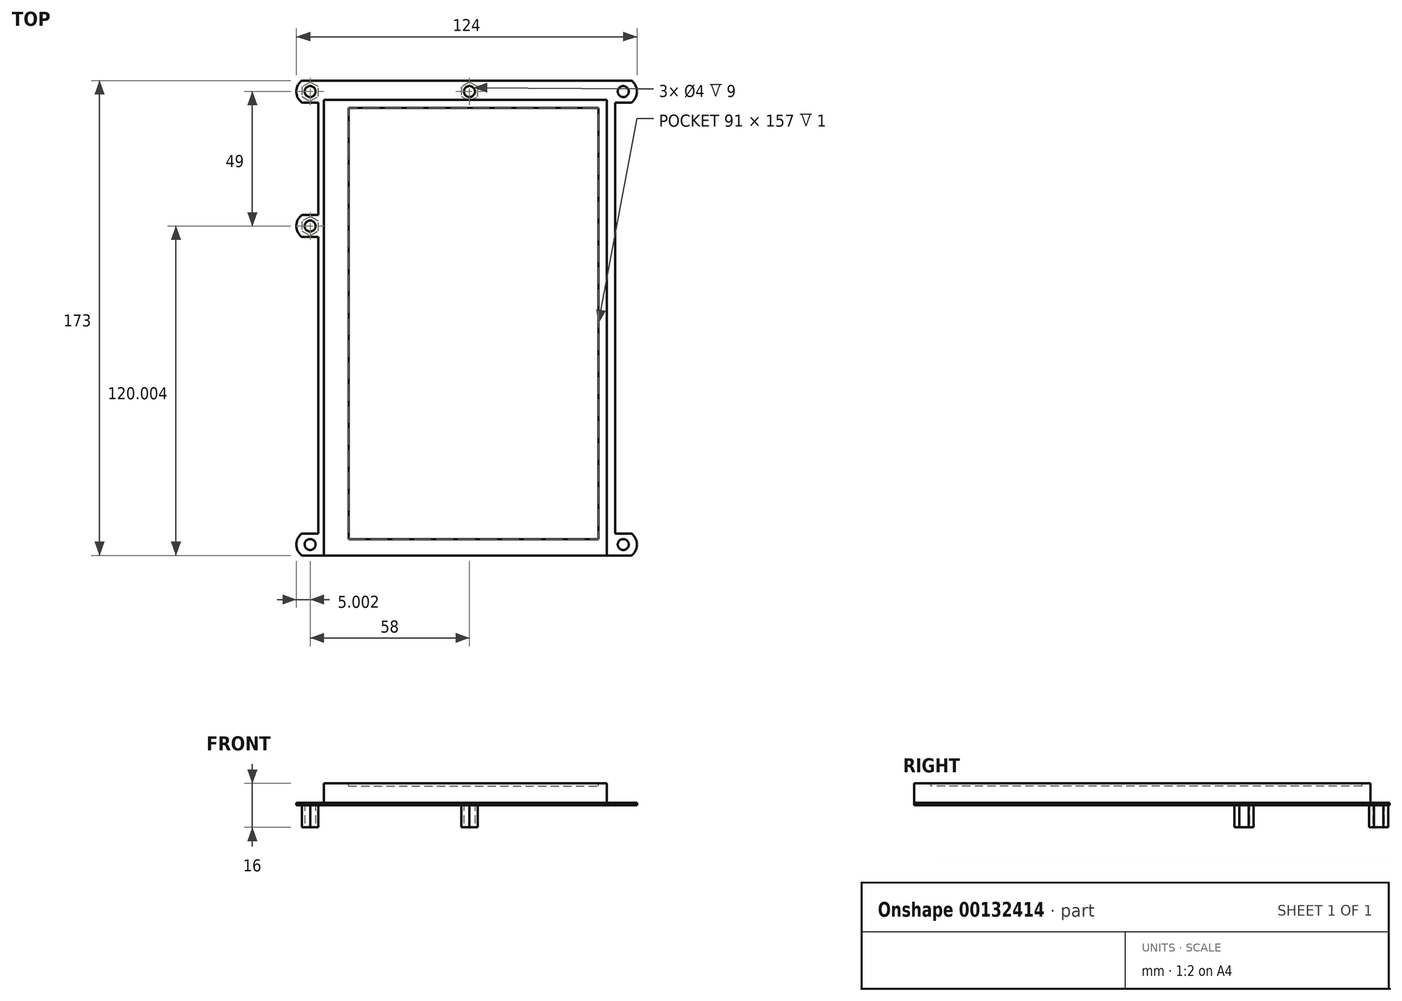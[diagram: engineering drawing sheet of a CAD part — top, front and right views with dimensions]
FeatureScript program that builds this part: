
annotation { "Feature Type Name" : "Feature", "Feature Type Description" : "" }
export const myFeature = defineFeature(function(context is Context, id is Id, definition is map)
    precondition{}
    {
        {
            var Q0;
            Q0=qCreatedBy(makeId("Top.planeOp"),FACE);
            var sketch = newSketch(context, id + "F0", { "sketchPlane" : qUnion([Q0])});
            skLineSegment(sketch, "E0.bottom", {"start": v(-61.72, 83.97) * mm, "end": v(58.28, 83.97) * mm});
            skLineSegment(sketch, "E0.top", {"start": v(-61.72, -89.03) * mm, "end": v(58.28, -89.03) * mm});
            skLineSegment(sketch, "E1", {"start": v(-61.72, -81.03) * mm, "end": v(-55.72, -81.03) * mm});
            skLineSegment(sketch, "E2", {"start": v(-55.72, -81.03) * mm, "end": v(-55.72, 26.97) * mm});
            skLineSegment(sketch, "E3", {"start": v(-55.72, 26.97) * mm, "end": v(-61.72, 26.97) * mm});
            skLineSegment(sketch, "E4", {"start": v(-61.72, 34.97) * mm, "end": v(-55.72, 34.97) * mm});
            skLineSegment(sketch, "E5", {"start": v(-55.72, 34.97) * mm, "end": v(-55.72, 75.97) * mm});
            skLineSegment(sketch, "E6", {"start": v(-55.72, 75.97) * mm, "end": v(-61.72, 75.97) * mm});
            skLineSegment(sketch, "E7", {"start": v(58.28, 75.97) * mm, "end": v(52.28, 75.97) * mm});
            skLineSegment(sketch, "E8", {"start": v(52.28, 75.97) * mm, "end": v(52.28, -81.03) * mm});
            skLineSegment(sketch, "E9", {"start": v(52.28, -81.03) * mm, "end": v(58.28, -81.03) * mm});
            skArc(sketch, "E10", {"start": v(58.28, 75.97) * mm, "mid": v(60.28, 79.97) * mm, "end": v(58.28, 83.97) * mm});
            skArc(sketch, "E11", {"start": v(-61.72, 34.97) * mm, "mid": v(-63.72, 30.97) * mm, "end": v(-61.72, 26.97) * mm});
            skArc(sketch, "E12", {"start": v(-61.72, 83.97) * mm, "mid": v(-63.72, 79.97) * mm, "end": v(-61.72, 75.97) * mm});
            skArc(sketch, "E13", {"start": v(-61.72, -81.03) * mm, "mid": v(-63.72, -85.03) * mm, "end": v(-61.72, -89.03) * mm});
            skArc(sketch, "E14", {"start": v(58.28, -89.03) * mm, "mid": v(60.28, -85.03) * mm, "end": v(58.28, -81.03) * mm});
            skCircle(sketch, "E15", {"center": v(55.28, -85.03) * mm, "radius": 2 * mm});
            skCircle(sketch, "E16", {"center": v(-58.72, -85.03) * mm, "radius": 2 * mm});
            skCircle(sketch, "E17", {"center": v(-58.72, 30.97) * mm, "radius": 2 * mm});
            skCircle(sketch, "E18", {"center": v(-58.72, 79.97) * mm, "radius": 2 * mm});
            skCircle(sketch, "E19", {"center": v(55.28, 79.97) * mm, "radius": 2 * mm});
            skSolve(sketch);
        }
        {
            var Q0;
            Q0=makeQuery(id+"F0.imprint","IMPRINT",FACE,{"disambiguationData":[TD([[makeQuery(id+"F0.imprint","IMPRINT",EDGE,{"derivedFrom":sQuery(id+"F0.wireOp",EDGE,"E0.bottom")}),-1.0]])]});
            extrude(context, id + "F1", {"entities" : qUnion([Q0]), "depth" : 1 * mm});
        }
        {
            var Q0;
            Q0=makeQuery(id+"F1.opExtrude","CAP_FACE",FACE,{"disambiguationData":[OSD([sQuery(id+"F0.wireOp",EDGE,"E0.bottom"),sQuery(id+"F0.wireOp",EDGE,"E0.top"),sQuery(id+"F0.wireOp",EDGE,"E1"),sQuery(id+"F0.wireOp",EDGE,"E2"),sQuery(id+"F0.wireOp",EDGE,"E3"),sQuery(id+"F0.wireOp",EDGE,"E4"),sQuery(id+"F0.wireOp",EDGE,"E5"),sQuery(id+"F0.wireOp",EDGE,"E6"),sQuery(id+"F0.wireOp",EDGE,"E7"),sQuery(id+"F0.wireOp",EDGE,"E8"),sQuery(id+"F0.wireOp",EDGE,"E9"),sQuery(id+"F0.wireOp",EDGE,"E10"),sQuery(id+"F0.wireOp",EDGE,"E11"),sQuery(id+"F0.wireOp",EDGE,"E12"),sQuery(id+"F0.wireOp",EDGE,"E13"),sQuery(id+"F0.wireOp",EDGE,"E14"),sQuery(id+"F0.wireOp",EDGE,"E15"),sQuery(id+"F0.wireOp",EDGE,"E16"),sQuery(id+"F0.wireOp",EDGE,"E17"),sQuery(id+"F0.wireOp",EDGE,"E18"),sQuery(id+"F0.wireOp",EDGE,"E19")])],"isStart":false});
            var sketch = newSketch(context, id + "F2", { "sketchPlane" : qUnion([Q0])});
            skLineSegment(sketch, "E20", {"start": v(-53.72, 76.97) * mm, "end": v(49.28, 76.97) * mm});
            skLineSegment(sketch, "E21", {"start": v(49.28, 76.97) * mm, "end": v(49.28, -89.03) * mm});
            skLineSegment(sketch, "E22", {"start": v(-53.72, 76.97) * mm, "end": v(-53.72, -89.03) * mm});
            skLineSegment(sketch, "E23.0", {"start": v(-53.72, -89.03) * mm, "end": v(49.28, -89.03) * mm});
            skPoint(sketch, "E24.orphan", {"position": v(58.28, -89.03) * mm});
            skPoint(sketch, "E25.orphan", {"position": v(-61.72, -89.03) * mm});
            skSolve(sketch);
        }
        {
            var Q0;
            Q0 = qSketchRegion(id + "F2", true);
            extrude(context, id + "F3", {"entities" : qUnion([Q0]), "depth" : 7 * mm});
        }
        {
            var Q0;
            Q0=makeQuery(id+"F3.opExtrude","CAP_FACE",FACE,{"disambiguationData":[OSD([sQuery(id+"F2.wireOp",EDGE,"E20"),sQuery(id+"F2.wireOp",EDGE,"E21"),sQuery(id+"F2.wireOp",EDGE,"E22"),sQuery(id+"F2.wireOp",EDGE,"E23.0")])],"isStart":false});
            var sketch = newSketch(context, id + "F4", { "sketchPlane" : qUnion([Q0])});
            skLineSegment(sketch, "E26.bottom", {"start": v(-44.72, 73.97) * mm, "end": v(46.28, 73.97) * mm});
            skLineSegment(sketch, "E26.top", {"start": v(-44.72, -83.03) * mm, "end": v(46.28, -83.03) * mm});
            skLineSegment(sketch, "E26.left", {"start": v(-44.72, 73.97) * mm, "end": v(-44.72, -83.03) * mm});
            skLineSegment(sketch, "E26.right", {"start": v(46.28, 73.97) * mm, "end": v(46.28, -83.03) * mm});
            skSolve(sketch);
        }
        {
            var Q0;
            Q0=makeQuery(id+"F4.imprint","IMPRINT",FACE,{"disambiguationData":[TD([[makeQuery(id+"F4.imprint","IMPRINT",EDGE,{"derivedFrom":sQuery(id+"F4.wireOp",EDGE,"E26.bottom")}),-1.0]])]});
            extrude(context, id + "F5", {"entities" : qUnion([Q0]), "operationType" : NewBodyOperationType.REMOVE, "oppositeDirection" : true, "depth" : 1 * mm});
        }
        {
            var Q0;
            Q0=makeQuery(id+"F1.opExtrude","CAP_FACE",FACE,{"disambiguationData":[OSD([sQuery(id+"F0.wireOp",EDGE,"E0.bottom"),sQuery(id+"F0.wireOp",EDGE,"E0.top"),sQuery(id+"F0.wireOp",EDGE,"E1"),sQuery(id+"F0.wireOp",EDGE,"E2"),sQuery(id+"F0.wireOp",EDGE,"E3"),sQuery(id+"F0.wireOp",EDGE,"E4"),sQuery(id+"F0.wireOp",EDGE,"E5"),sQuery(id+"F0.wireOp",EDGE,"E6"),sQuery(id+"F0.wireOp",EDGE,"E7"),sQuery(id+"F0.wireOp",EDGE,"E8"),sQuery(id+"F0.wireOp",EDGE,"E9"),sQuery(id+"F0.wireOp",EDGE,"E10"),sQuery(id+"F0.wireOp",EDGE,"E11"),sQuery(id+"F0.wireOp",EDGE,"E12"),sQuery(id+"F0.wireOp",EDGE,"E13"),sQuery(id+"F0.wireOp",EDGE,"E14"),sQuery(id+"F0.wireOp",EDGE,"E15"),sQuery(id+"F0.wireOp",EDGE,"E16"),sQuery(id+"F0.wireOp",EDGE,"E17"),sQuery(id+"F0.wireOp",EDGE,"E18"),sQuery(id+"F0.wireOp",EDGE,"E19")])],"isStart":true});
            var sketch = newSketch(context, id + "F6", { "sketchPlane" : qUnion([Q0])});
            skCircle(sketch, "E27", {"center": v(-0.72, -79.97) * mm, "radius": 2 * mm});
            skSolve(sketch);
        }
        {
            var Q0;
            Q0 = qSketchRegion(id + "F6", true);
            extrude(context, id + "F7", {"entities" : qUnion([Q0]), "operationType" : NewBodyOperationType.REMOVE, "endBound" : BoundingType.THROUGH_ALL, "oppositeDirection" : true, "depth" : 25 * mm});
        }
        {
            var Q0;
            Q0=makeQuery(id+"F1.opExtrude","CAP_FACE",FACE,{"disambiguationData":[OSD([sQuery(id+"F0.wireOp",EDGE,"E0.bottom"),sQuery(id+"F0.wireOp",EDGE,"E0.top"),sQuery(id+"F0.wireOp",EDGE,"E1"),sQuery(id+"F0.wireOp",EDGE,"E2"),sQuery(id+"F0.wireOp",EDGE,"E3"),sQuery(id+"F0.wireOp",EDGE,"E4"),sQuery(id+"F0.wireOp",EDGE,"E5"),sQuery(id+"F0.wireOp",EDGE,"E6"),sQuery(id+"F0.wireOp",EDGE,"E7"),sQuery(id+"F0.wireOp",EDGE,"E8"),sQuery(id+"F0.wireOp",EDGE,"E9"),sQuery(id+"F0.wireOp",EDGE,"E10"),sQuery(id+"F0.wireOp",EDGE,"E11"),sQuery(id+"F0.wireOp",EDGE,"E12"),sQuery(id+"F0.wireOp",EDGE,"E13"),sQuery(id+"F0.wireOp",EDGE,"E14"),sQuery(id+"F0.wireOp",EDGE,"E15"),sQuery(id+"F0.wireOp",EDGE,"E16"),sQuery(id+"F0.wireOp",EDGE,"E17"),sQuery(id+"F0.wireOp",EDGE,"E18"),sQuery(id+"F0.wireOp",EDGE,"E19")])],"isStart":true});
            var sketch = newSketch(context, id + "F8", { "sketchPlane" : qUnion([Q0])});
            skCircle(sketch, "E28.cCircle", {"center": v(-0.72, -79.97) * mm, "radius": 3 * mm, "construction": true});
            skLineSegment(sketch, "E28.0", {"start": v(-3.72, -81.7) * mm, "end": v(-3.72, -78.24) * mm});
            skLineSegment(sketch, "E28.1", {"start": v(-3.72, -78.24) * mm, "end": v(-0.72, -76.5) * mm});
            skLineSegment(sketch, "E28.2", {"start": v(-0.72, -76.5) * mm, "end": v(2.28, -78.24) * mm});
            skLineSegment(sketch, "E28.3", {"start": v(2.28, -78.24) * mm, "end": v(2.28, -81.7) * mm});
            skLineSegment(sketch, "E28.4", {"start": v(2.28, -81.7) * mm, "end": v(-0.72, -83.44) * mm});
            skLineSegment(sketch, "E28.5", {"start": v(-0.72, -83.44) * mm, "end": v(-3.72, -81.7) * mm});
            skPoint(sketch, "E28.0.midPoint", {"position": v(-3.72, -79.97) * mm});
            skCircle(sketch, "E29.0", {"center": v(-0.72, -79.97) * mm, "radius": 2 * mm});
            skCircle(sketch, "E30.cCircle", {"center": v(-58.72, -79.97) * mm, "radius": 3 * mm, "construction": true});
            skLineSegment(sketch, "E30.0", {"start": v(-61.72, -81.7) * mm, "end": v(-61.72, -78.24) * mm});
            skLineSegment(sketch, "E30.1", {"start": v(-61.72, -78.24) * mm, "end": v(-58.72, -76.5) * mm});
            skLineSegment(sketch, "E30.2", {"start": v(-58.72, -76.5) * mm, "end": v(-55.72, -78.24) * mm});
            skLineSegment(sketch, "E30.3", {"start": v(-55.72, -78.24) * mm, "end": v(-55.72, -81.7) * mm});
            skLineSegment(sketch, "E30.4", {"start": v(-55.72, -81.7) * mm, "end": v(-58.72, -83.44) * mm});
            skLineSegment(sketch, "E30.5", {"start": v(-58.72, -83.44) * mm, "end": v(-61.72, -81.7) * mm});
            skPoint(sketch, "E30.0.midPoint", {"position": v(-61.72, -79.97) * mm});
            skCircle(sketch, "E31.0", {"center": v(-58.72, -79.97) * mm, "radius": 2 * mm});
            skCircle(sketch, "E32.cCircle", {"center": v(-58.72, -30.97) * mm, "radius": 3 * mm, "construction": true});
            skLineSegment(sketch, "E32.0", {"start": v(-61.72, -32.7) * mm, "end": v(-61.72, -29.24) * mm});
            skLineSegment(sketch, "E32.1", {"start": v(-61.72, -29.24) * mm, "end": v(-58.72, -27.5) * mm});
            skLineSegment(sketch, "E32.2", {"start": v(-58.72, -27.5) * mm, "end": v(-55.72, -29.24) * mm});
            skLineSegment(sketch, "E32.3", {"start": v(-55.72, -29.24) * mm, "end": v(-55.72, -32.7) * mm});
            skLineSegment(sketch, "E32.4", {"start": v(-55.72, -32.7) * mm, "end": v(-58.72, -34.44) * mm});
            skLineSegment(sketch, "E32.5", {"start": v(-58.72, -34.44) * mm, "end": v(-61.72, -32.7) * mm});
            skPoint(sketch, "E32.0.midPoint", {"position": v(-61.72, -30.97) * mm});
            skCircle(sketch, "E33.0", {"center": v(-58.72, -30.97) * mm, "radius": 2 * mm});
            skSolve(sketch);
        }
        {
            var Q0;
            Q0 = qSketchRegion(id + "F8", true);
            extrude(context, id + "F9", {"entities" : qUnion([Q0]), "operationType" : NewBodyOperationType.ADD, "depth" : 8 * mm});
        }
    });
